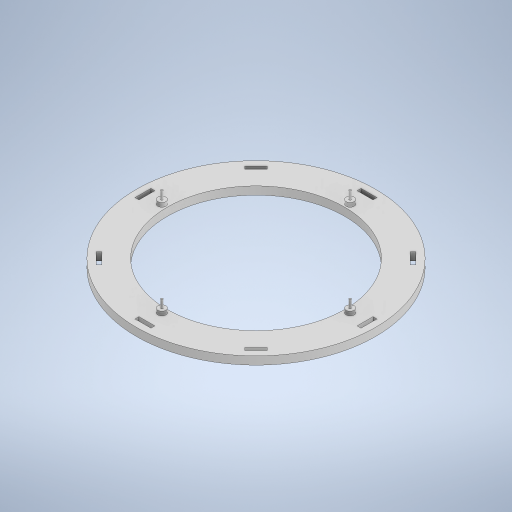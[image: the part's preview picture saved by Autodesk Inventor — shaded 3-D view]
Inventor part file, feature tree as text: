
AUTODESK INVENTOR PART (.ipt)
format: ipt  version: 2023 (Build 270158000, 158)  size: 296,448 bytes
history: native  units: in
note: dims shown in document units (in); Inventor stores cm internally (conversion verified against a paired STEP export)
features: extrude x5, sketch x5, pattern_circular x2
ambient origin geometry x8: Origin, YZ Plane, XZ Plane, XY Plane, X Axis, Y Axis, Z Axis, Center Point
bodies: Solid1 (feature_tree)
feature tree (12):
  extrude  "Extrusion1"  Depth=0.3937in TaperAngle=0.0deg
  sketch  "Sketch3"  dims[d4=8.7598in d5=9.3012in]
  extrude  "Extrusion2"  Depth=9.3012in
  extrude  "Extrusion3"  Depth=0.5906in TaperAngle=0.0deg
  extrude  "Extrusion4"  Depth=0.1969in TaperAngle=0.0deg
  pattern_circular  "Circular Pattern1"  Count=4 Angle=360.0deg
  extrude  "Extrusion5"  Depth=0.3937in
  pattern_circular  "Circular Pattern2"  [2 undecoded]
  sketch  "Sketch2"  dims[d1=11.811in d2=0.3937in d3=0.0in]
  sketch  "Sketch4"  dims[d6=0.0984in d7=0.5906in d8=0.0in]
  sketch  "Sketch5"  dims[d9=0.3937in d10=0.1969in d11=0.0in]
  sketch  "Sketch6"  dims[d12=0.3937in d13=0.0in d14=1.5748in d15=360.0deg d17=0.3937in d18=0.0in d19=0.0984in d20=0.7874in d21=0.1969in d22=0.0in d23=0.0in d24=3.1496in d25=360.0deg]
note: 2 required parameter values undecoded (feature->parameter linkage not recoverable at this tier; creation-order binding heuristic only, values carry confidence <= 0.55)
